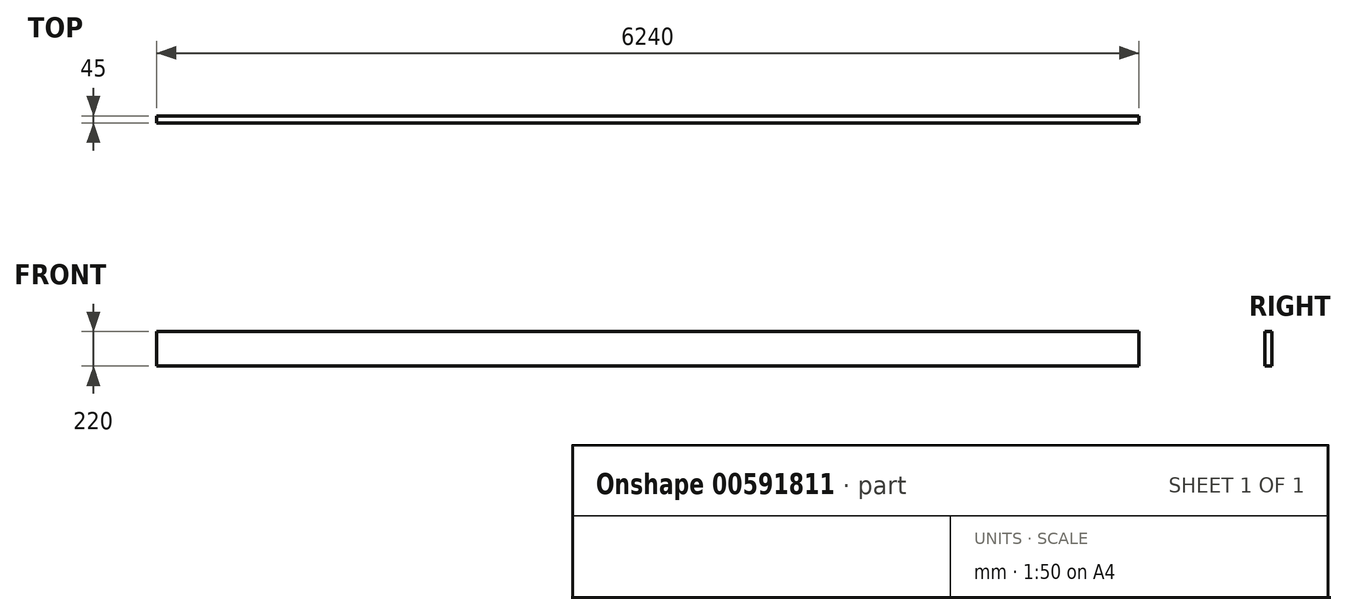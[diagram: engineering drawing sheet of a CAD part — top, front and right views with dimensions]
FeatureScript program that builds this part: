
annotation { "Feature Type Name" : "Feature", "Feature Type Description" : "" }
export const myFeature = defineFeature(function(context is Context, id is Id, definition is map)
    precondition{}
    {
        {
            var Q0;
            Q0=qCreatedBy(makeId("Front.planeOp"),FACE);
            var sketch = newSketch(context, id + "F0", { "sketchPlane" : qUnion([Q0])});
            skLineSegment(sketch, "E0.bottom", {"start": v(0, 0) * mm, "end": v(6240, 0) * mm});
            skLineSegment(sketch, "E0.top", {"start": v(0, 220) * mm, "end": v(6240, 220) * mm});
            skLineSegment(sketch, "E0.left", {"start": v(0, 0) * mm, "end": v(0, 220) * mm});
            skLineSegment(sketch, "E0.right", {"start": v(6240, 0) * mm, "end": v(6240, 220) * mm});
            skSolve(sketch);
        }
        {
            var Q0;
            Q0=makeQuery(id+"F0.imprint","IMPRINT",FACE,{"disambiguationData":[TD([[makeQuery(id+"F0.imprint","IMPRINT",EDGE,{"derivedFrom":sQuery(id+"F0.wireOp",EDGE,"E0.bottom")}),1.0]])]});
            extrude(context, id + "F1", {"entities" : qUnion([Q0]), "depth" : 45 * mm, "offsetDistance" : 25 * mm});
        }
    });
